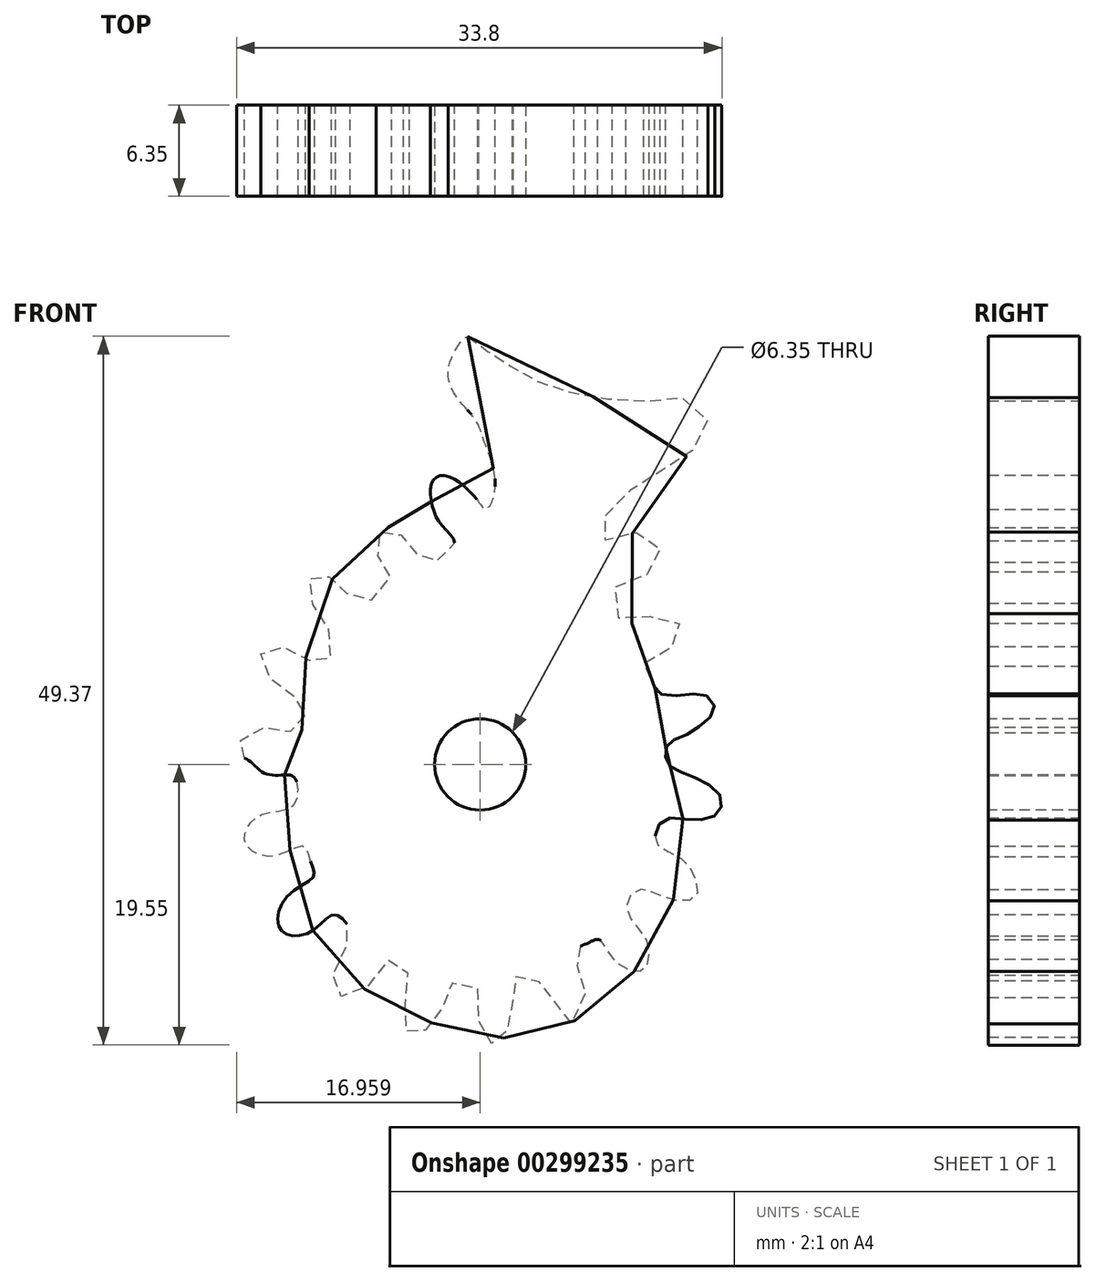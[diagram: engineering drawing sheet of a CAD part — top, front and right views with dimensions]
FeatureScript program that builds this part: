
annotation { "Feature Type Name" : "Feature", "Feature Type Description" : "" }
export const myFeature = defineFeature(function(context is Context, id is Id, definition is map)
    precondition{}
    {
        {
            var Q0;
            Q0=qCreatedBy(makeId("Front.planeOp"),FACE);
            var sketch = newSketch(context, id + "F0", { "sketchPlane" : qUnion([Q0])});
            skFitSpline(sketch, "E0", {"points": [v(18.27, 51.31) * mm, v(18.92, 50.85) * mm, v(19.89, 50.12) * mm, v(20.85, 49.52) * mm, v(21.82, 48.87) * mm, v(23.43, 48.04) * mm, v(25.14, 47.49) * mm, v(27.17, 47.07) * mm, v(29.56, 46.84) * mm, v(31.78, 46.9) * mm, v(33.62, 46.94) * mm, v(34.96, 45.5) * mm, v(34.36, 43.9) * mm, v(32.93, 42.56) * mm, v(30.9, 41.54) * mm, v(29.2, 40.25) * mm, v(27.77, 38.73) * mm, v(27.35, 37.44) * mm, v(28.46, 37.12) * mm, v(30.12, 37.67) * mm, v(31.55, 36.98) * mm, v(31.45, 35.6) * mm, v(30.58, 34.63) * mm, v(28.64, 33.94) * mm, v(28.32, 33.2) * mm, v(29.06, 31.4) * mm, v(30.85, 31.77) * mm, v(32.47, 31.82) * mm, v(33.25, 30.48) * mm, v(32.47, 29.65) * mm, v(30.8, 28.82) * mm, v(30.53, 28.13) * mm, v(31.09, 27.16) * mm, v(31.64, 26.43) * mm, v(33.44, 26.33) * mm, v(34.86, 26.29) * mm, v(35.46, 25.37) * mm, v(34.59, 24.3) * mm, v(33.39, 23.52) * mm, v(32.24, 22.97) * mm, v(32.05, 22.37) * mm, v(32.15, 21.59) * mm, v(32.98, 21.03) * mm, v(34.45, 20.39) * mm, v(35.79, 19.42) * mm, v(35.88, 18.4) * mm, v(35.14, 17.76) * mm, v(33.44, 17.67) * mm, v(31.96, 17.67) * mm, v(31.32, 16.66) * mm, v(31.5, 15.87) * mm, v(33.02, 15) * mm, v(34.04, 13.75) * mm, v(34.13, 12.28) * mm, v(32.65, 12.05) * mm, v(31.22, 12.55) * mm, v(30.07, 12.74) * mm, v(29.29, 11.59) * mm, v(30.16, 10.02) * mm, v(30.85, 8.77) * mm, v(30.62, 7.3) * mm, v(29.93, 7.07) * mm, v(28.46, 7.85) * mm, v(27.44, 9.28) * mm, v(26.52, 9) * mm, v(25.7, 8.54) * mm, v(26.02, 7.12) * mm, v(26.43, 5.46) * mm, v(25.42, 3.43) * mm, v(24.63, 4.4) * mm, v(23.71, 5.96) * mm, v(22.24, 6.8) * mm, v(21.45, 6.56) * mm, v(21.4, 5.55) * mm, v(21.13, 3.3) * mm, v(20.25, 1.95) * mm, v(19.56, 2.41) * mm, v(18.96, 4.12) * mm, v(18.83, 6.1) * mm, v(17.17, 6.24) * mm, v(16.52, 4.67) * mm, v(15.78, 3.52) * mm, v(14.54, 2.5) * mm, v(13.9, 3.1) * mm, v(13.9, 4.76) * mm, v(14.12, 6.89) * mm, v(12.97, 7.95) * mm, v(11.82, 6.7) * mm, v(10.02, 5.27) * mm, v(8.87, 5.82) * mm, v(9.1, 7.44) * mm, v(10.02, 9.33) * mm, v(9.93, 10.2) * mm, v(8.96, 11.03) * mm, v(7.53, 9.97) * mm, v(5.78, 9.6) * mm, v(5.05, 10.43) * mm, v(5.78, 12.42) * mm, v(7.53, 13.7) * mm, v(7.35, 14.63) * mm, v(6.84, 15.78) * mm, v(4.63, 15.09) * mm, v(2.79, 15.96) * mm, v(2.93, 17.12) * mm, v(4.12, 18.08) * mm, v(6.2, 18.73) * mm, v(6.2, 20.57) * mm, v(5.41, 20.76) * mm, v(3.99, 20.94) * mm, v(2.88, 21.86) * mm, v(2.19, 22.23) * mm, v(2.74, 23.57) * mm, v(4.08, 24.08) * mm, v(5.5, 23.94) * mm, v(6.61, 23.8) * mm, v(6.89, 25.74) * mm, v(6.47, 26.06) * mm, v(4.9, 27.03) * mm, v(3.94, 28.55) * mm, v(3.99, 29.47) * mm, v(5.5, 29.65) * mm, v(7.03, 28.92) * mm, v(8.04, 28.36) * mm, v(9.06, 29.93) * mm, v(8.13, 31.4) * mm, v(7.35, 33.02) * mm, v(7.26, 34.3) * mm, v(7.72, 34.9) * mm, v(9.1, 34.22) * mm, v(9.75, 33.52) * mm, v(10.71, 32.74) * mm, v(12.93, 34.12) * mm, v(12.51, 35) * mm, v(11.96, 36.2) * mm, v(12, 37.44) * mm, v(12.74, 38) * mm, v(13.9, 37.17) * mm, v(14.63, 36.24) * mm, v(15.5, 35.6) * mm, v(16.61, 35.97) * mm, v(17.35, 36.93) * mm, v(16.43, 38.18) * mm, v(15.74, 39.7) * mm, v(15.78, 41.18) * mm, v(16.52, 41.64) * mm, v(18.04, 40.85) * mm, v(19.15, 39.6) * mm, v(19.52, 39.29) * mm, v(19.98, 39.88) * mm, v(20.16, 41.22) * mm, v(19.89, 42.7) * mm, v(19.42, 43.94) * mm, v(18.87, 45.37) * mm, v(17.81, 46.66) * mm, v(16.98, 48.09) * mm, v(17.12, 49.8) * mm, v(18.27, 51.31) * mm]});
            skSolve(sketch);
        }
        {
            var Q0;
            Q0=makeQuery(id+"F0.imprint","IMPRINT",FACE,{"disambiguationData":[TD([[makeQuery(id+"F0.imprint","IMPRINT",EDGE,{"derivedFrom":sQuery(id+"F0.wireOp",EDGE,"E0")}),-1.0]])]});
            extrude(context, id + "F1", {"entities" : qUnion([Q0]), "depth" : 6.35 * mm});
        }
        {
            var Q0;
            Q0=makeQuery(id+"F1.opExtrude","CAP_FACE",FACE,{"disambiguationData":[OSD([sQuery(id+"F0.wireOp",EDGE,"E0")])],"isStart":false});
            var sketch = newSketch(context, id + "F2", { "sketchPlane" : qUnion([Q0])});
            skCircle(sketch, "E1", {"center": v(19.12, 21.5) * mm, "radius": 3.18 * mm});
            skSolve(sketch);
        }
        {
            var Q0;
            Q0 = qSketchRegion(id + "F2", true);
            extrude(context, id + "F3", {"entities" : qUnion([Q0]), "operationType" : NewBodyOperationType.REMOVE, "oppositeDirection" : true, "depth" : 25.4 * mm});
        }
    });
